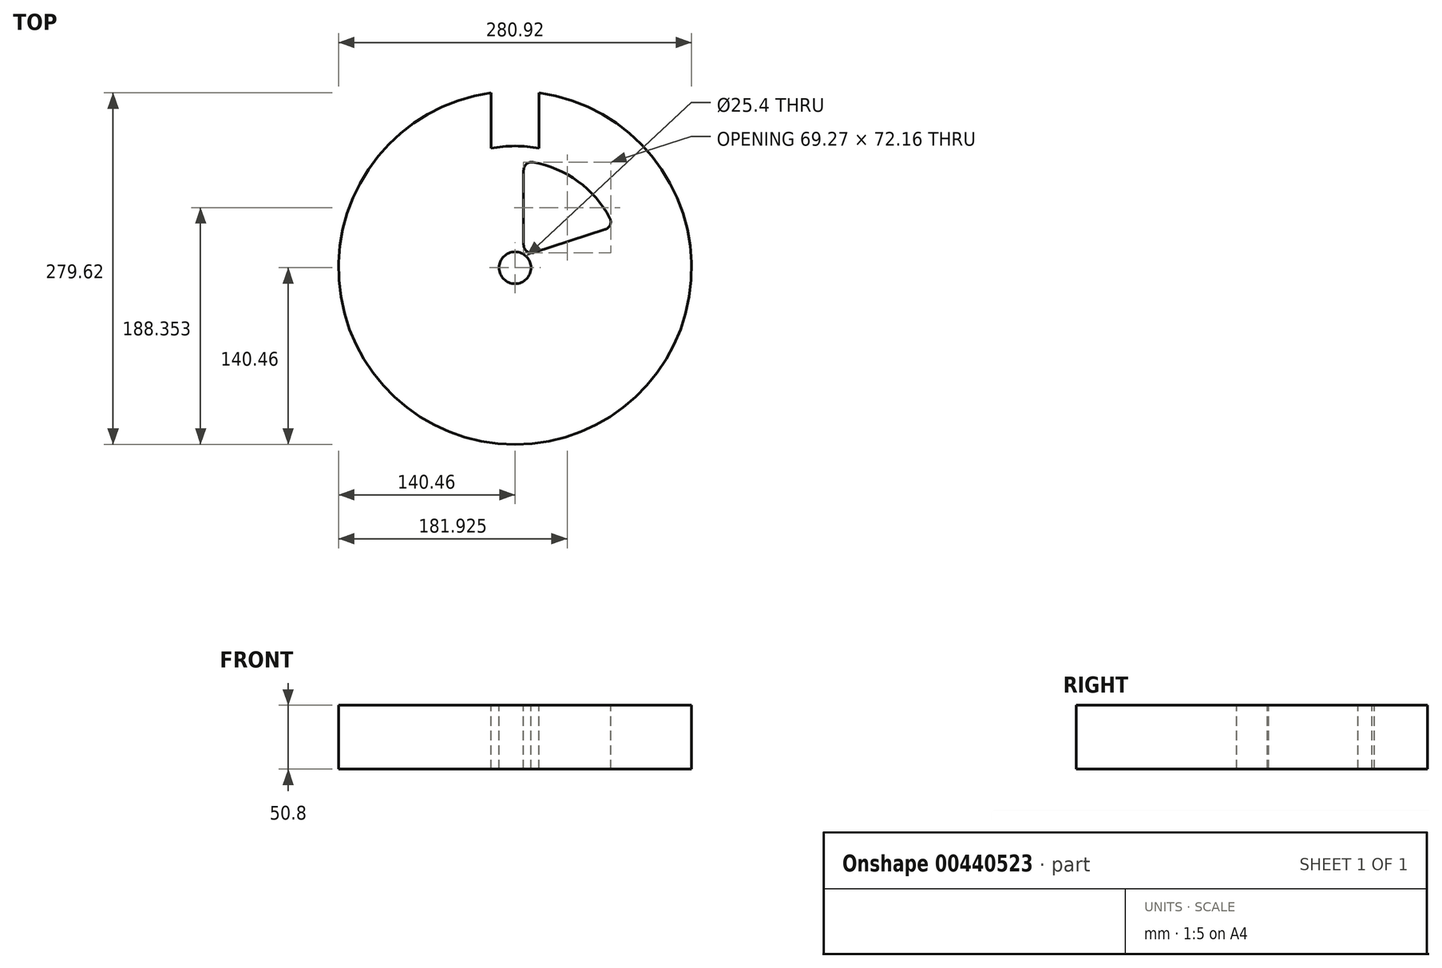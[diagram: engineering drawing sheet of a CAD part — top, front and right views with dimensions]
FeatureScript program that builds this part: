
annotation { "Feature Type Name" : "Feature", "Feature Type Description" : "" }
export const myFeature = defineFeature(function(context is Context, id is Id, definition is map)
    precondition{}
    {
        {
            var Q0;
            Q0=qCreatedBy(makeId("Top.planeOp"),FACE);
            var sketch = newSketch(context, id + "F0", { "sketchPlane" : qUnion([Q0])});
            skCircle(sketch, "E0", {"center": v(0, 0) * mm, "radius": 140.46 * mm});
            skSolve(sketch);
        }
        {
            var Q0;
            Q0=qSketchRegion(id+"F0",true);
            extrude(context, id + "F1", {"entities" : qUnion([Q0]), "endBound" : BoundingType.SYMMETRIC, "depth" : 50.8 * mm});
        }
        {
            var Q0;
            Q0=makeQuery(id+"F1.opExtrude","CAP_FACE",FACE,{"disambiguationData":[OSD([sQuery(id+"F0.wireOp",EDGE,"E0")])],"isStart":false});
            var sketch = newSketch(context, id + "F2", { "sketchPlane" : qUnion([Q0])});
            skArc(sketch, "E1", {"start": v(19.05, 94.95) * mm, "mid": v(0, 96.84) * mm, "end": v(-19.05, 94.95) * mm});
            skLineSegment(sketch, "E2", {"start": v(-19.05, 94.95) * mm, "end": v(-19.05, 139.16) * mm});
            skLineSegment(sketch, "E3", {"start": v(19.05, 94.95) * mm, "end": v(19.05, 139.16) * mm});
            skArc(sketch, "E4", {"start": v(19.05, 139.16) * mm, "mid": v(0, 140.46) * mm, "end": v(-19.05, 139.16) * mm});
            skSolve(sketch);
        }
        {
            var Q0;
            Q0=qSketchRegion(id+"F2",true);
            extrude(context, id + "F3", {"entities" : qUnion([Q0]), "operationType" : NewBodyOperationType.REMOVE, "endBound" : BoundingType.THROUGH_ALL, "oppositeDirection" : true, "depth" : 25.4 * mm});
        }
        {
            var Q0;
            Q0=qCreatedBy(makeId("Right.planeOp"),FACE);
            var sketch = newSketch(context, id + "F4", { "sketchPlane" : qUnion([Q0])});
            skLineSegment(sketch, "E5", {"start": v(0, 64.1) * mm, "end": v(0, -44.44) * mm});
            skSolve(sketch);
        }
        {
            var Q0;
            Q0=makeQuery(id+"F1.opExtrude","CAP_FACE",FACE,{"disambiguationData":[OSD([sQuery(id+"F0.wireOp",EDGE,"E0")])],"isStart":false});
            var sketch = newSketch(context, id + "F5", { "sketchPlane" : qUnion([Q0])});
            skArc(sketch, "E6", {"start": v(75.38, 39.47) * mm, "mid": v(50.01, 68.84) * mm, "end": v(14.25, 83.89) * mm});
            skLineSegment(sketch, "E7", {"start": v(6.83, 77.63) * mm, "end": v(6.83, 18.14) * mm});
            skLineSegment(sketch, "E8", {"start": v(15.14, 12.1) * mm, "end": v(71.72, 30.49) * mm});
            skPoint(sketch, "E9.visualSharp", {"position": v(6.83, 9.4) * mm});
            skArc(sketch, "E9.filletArc", {"start": v(6.83, 18.14) * mm, "mid": v(9.45, 13) * mm, "end": v(15.14, 12.1) * mm});
            skPoint(sketch, "E10.visualSharp", {"position": v(6.83, 84.82) * mm});
            skArc(sketch, "E10.filletArc", {"start": v(14.25, 83.89) * mm, "mid": v(9.09, 82.48) * mm, "end": v(6.83, 77.63) * mm});
            skPoint(sketch, "E11.visualSharp", {"position": v(78.55, 32.7) * mm});
            skArc(sketch, "E11.filletArc", {"start": v(71.72, 30.49) * mm, "mid": v(75.64, 34.13) * mm, "end": v(75.38, 39.47) * mm});
            skPoint(sketch, "E12.center.orphan", {"position": v(0, 2.6) * mm});
            skSolve(sketch);
        }
        {
            var Q0;
            Q0=qSketchRegion(id+"F5",true);
            extrude(context, id + "F6", {"entities" : qUnion([Q0]), "operationType" : NewBodyOperationType.REMOVE, "endBound" : BoundingType.THROUGH_ALL, "oppositeDirection" : true, "depth" : 25.4 * mm});
        }
        {
            var Q0;
            Q0=makeQuery(id+"F1.opExtrude","CAP_FACE",FACE,{"disambiguationData":[OSD([sQuery(id+"F0.wireOp",EDGE,"E0")])],"isStart":false});
            var sketch = newSketch(context, id + "F7", { "sketchPlane" : qUnion([Q0])});
            skCircle(sketch, "E13", {"center": v(0, 0) * mm, "radius": 12.7 * mm});
            skSolve(sketch);
        }
        {
            var Q0;
            Q0=qSketchRegion(id+"F7",true);
            extrude(context, id + "F8", {"entities" : qUnion([Q0]), "operationType" : NewBodyOperationType.REMOVE, "endBound" : BoundingType.THROUGH_ALL, "oppositeDirection" : true, "depth" : 25.4 * mm});
        }
    });
